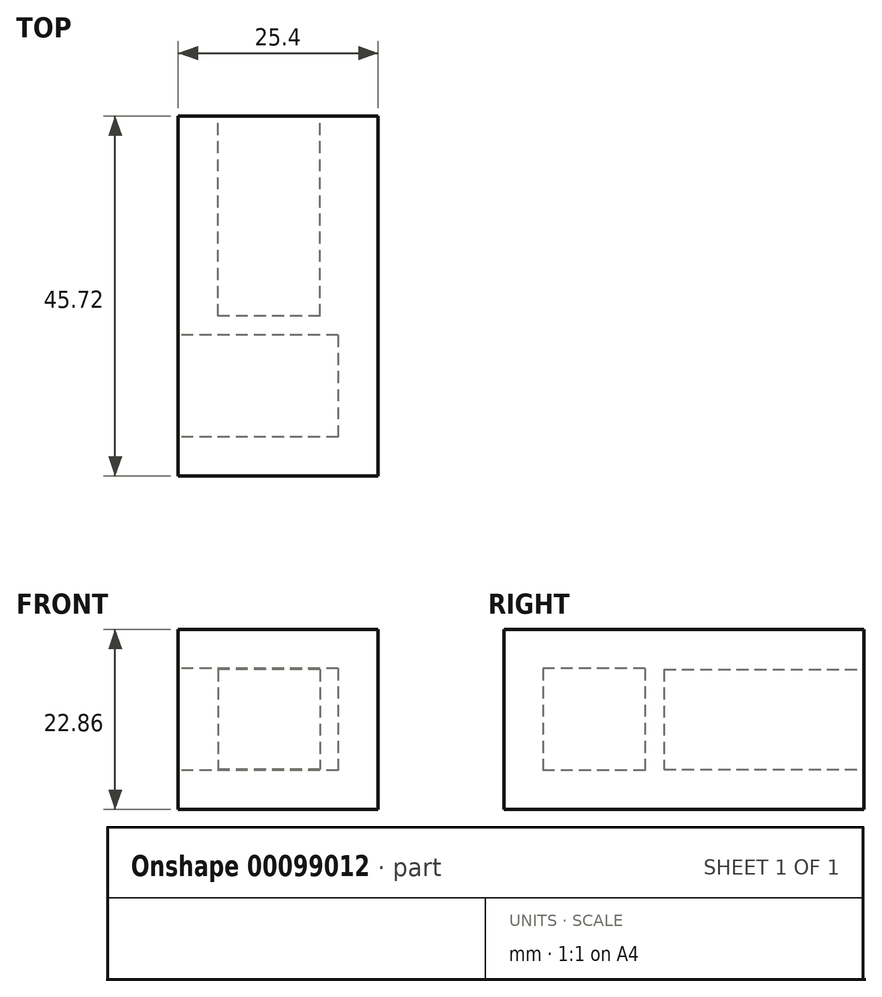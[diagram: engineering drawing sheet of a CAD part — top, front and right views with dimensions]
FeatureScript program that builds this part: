
annotation { "Feature Type Name" : "Feature", "Feature Type Description" : "" }
export const myFeature = defineFeature(function(context is Context, id is Id, definition is map)
    precondition{}
    {
        {
            var Q0;
            Q0=qCreatedBy(makeId("Right.planeOp"),FACE);
            var sketch = newSketch(context, id + "F0", { "sketchPlane" : qUnion([Q0])});
            skLineSegment(sketch, "E0.bottom", {"start": v(6.48, 6.48) * mm, "end": v(-6.48, 6.48) * mm});
            skLineSegment(sketch, "E0.top", {"start": v(6.48, -6.48) * mm, "end": v(-6.48, -6.48) * mm});
            skLineSegment(sketch, "E0.left", {"start": v(6.48, 6.48) * mm, "end": v(6.48, -6.48) * mm});
            skLineSegment(sketch, "E0.right", {"start": v(-6.48, 6.48) * mm, "end": v(-6.48, -6.48) * mm});
            skPoint(sketch, "E0.middle", {"position": v(0, 0) * mm});
            skLineSegment(sketch, "E1.bottom", {"start": v(11.43, 11.43) * mm, "end": v(-11.43, 11.43) * mm});
            skLineSegment(sketch, "E1.top", {"start": v(11.43, -11.43) * mm, "end": v(-11.43, -11.43) * mm});
            skLineSegment(sketch, "E1.left", {"start": v(11.43, 11.43) * mm, "end": v(11.43, -11.43) * mm});
            skLineSegment(sketch, "E1.right", {"start": v(-11.43, 11.43) * mm, "end": v(-11.43, -11.43) * mm});
            skSolve(sketch);
        }
        {
            var Q0;
            Q0=makeQuery(id+"F0.imprint","IMPRINT",FACE,{"disambiguationData":[TD([[makeQuery(id+"F0.imprint","IMPRINT",EDGE,{"derivedFrom":sQuery(id+"F0.wireOp",EDGE,"E0.bottom")}),-1.0]])]});
            extrude(context, id + "F1", {"entities" : qUnion([Q0]), "depth" : 25.4 * mm});
        }
        {
            var Q0;
            Q0=makeQuery(id+"F1.opExtrude","SWEPT_FACE",FACE,{"disambiguationData":[OSD([sQuery(id+"F0.wireOp",EDGE,"E1.left")])]});
            extrude(context, id + "F2", {"entities" : qUnion([Q0]), "operationType" : NewBodyOperationType.ADD, "depth" : 22.86 * mm});
        }
        {
            var Q0;
            {var subQ0=sQuery(id+"F0.wireOp",EDGE,"E1.left");Q0=makeQuery(id+"F2.boolean.opBoolean","MERGE",FACE,{"derivedFrom":[makeQuery(id+"F1.opExtrude","CAP_FACE",FACE,{"disambiguationData":[OSD([sQuery(id+"F0.wireOp",EDGE,"E0.bottom"),sQuery(id+"F0.wireOp",EDGE,"E0.top"),sQuery(id+"F0.wireOp",EDGE,"E0.left"),sQuery(id+"F0.wireOp",EDGE,"E0.right"),sQuery(id+"F0.wireOp",EDGE,"E1.bottom"),sQuery(id+"F0.wireOp",EDGE,"E1.top"),subQ0,sQuery(id+"F0.wireOp",EDGE,"E1.right")])],"isStart":false}),makeQuery(id+"F2.opExtrude","SWEPT_FACE",FACE,{"disambiguationData":[OSD([subQ0]),TDD([makeQuery(id+"F1.opExtrude","CAP_EDGE",EDGE,{"disambiguationData":[OSD([subQ0])],"isStart":false})])]})]});}
            var sketch = newSketch(context, id + "F3", { "sketchPlane" : qUnion([Q0])});
            skLineSegment(sketch, "E2.bottom", {"start": v(6.48, 6.48) * mm, "end": v(-6.48, 6.48) * mm});
            skLineSegment(sketch, "E2.top", {"start": v(6.48, -6.48) * mm, "end": v(-6.48, -6.48) * mm});
            skLineSegment(sketch, "E2.left", {"start": v(6.48, 6.48) * mm, "end": v(6.48, -6.48) * mm});
            skLineSegment(sketch, "E2.right", {"start": v(-6.48, 6.48) * mm, "end": v(-6.48, -6.48) * mm});
            skSolve(sketch);
        }
        {
            var Q0;
            Q0 = qSketchRegion(id + "F3", true);
            extrude(context, id + "F4", {"entities" : qUnion([Q0]), "operationType" : NewBodyOperationType.ADD, "oppositeDirection" : true, "depth" : 5.08 * mm});
        }
        {
            var Q0;
            Q0=makeQuery(id+"F2.opExtrude","CAP_FACE",FACE,{"disambiguationData":[OSD([sQuery(id+"F0.wireOp",EDGE,"E1.left")])],"isStart":false});
            var sketch = newSketch(context, id + "F5", { "sketchPlane" : qUnion([Q0])});
            skPoint(sketch, "E3", {"position": v(-4.83, 11.43) * mm});
            skPoint(sketch, "E4", {"position": v(-18.03, 11.43) * mm});
            skPoint(sketch, "E5", {"position": v(-25.4, 6.35) * mm});
            skPoint(sketch, "E6", {"position": v(-25.4, -6.35) * mm});
            skLineSegment(sketch, "E7.bottom", {"start": v(-18.03, 6.35) * mm, "end": v(-5.08, 6.35) * mm});
            skLineSegment(sketch, "E7.top", {"start": v(-18.03, -6.35) * mm, "end": v(-5.08, -6.35) * mm});
            skLineSegment(sketch, "E7.left", {"start": v(-18.03, 6.35) * mm, "end": v(-18.03, -6.35) * mm});
            skLineSegment(sketch, "E7.right", {"start": v(-5.08, 6.35) * mm, "end": v(-5.08, -6.35) * mm});
            skSolve(sketch);
        }
        {
            var Q0;
            Q0=makeQuery(id+"F5.imprint","IMPRINT",FACE,{"disambiguationData":[TD([[makeQuery(id+"F5.imprint","IMPRINT",EDGE,{"derivedFrom":sQuery(id+"F5.wireOp",EDGE,"E7.bottom")}),-1.0]])]});
            extrude(context, id + "F6", {"entities" : qUnion([Q0]), "operationType" : NewBodyOperationType.REMOVE, "oppositeDirection" : true, "depth" : 25.4 * mm});
        }
    });
